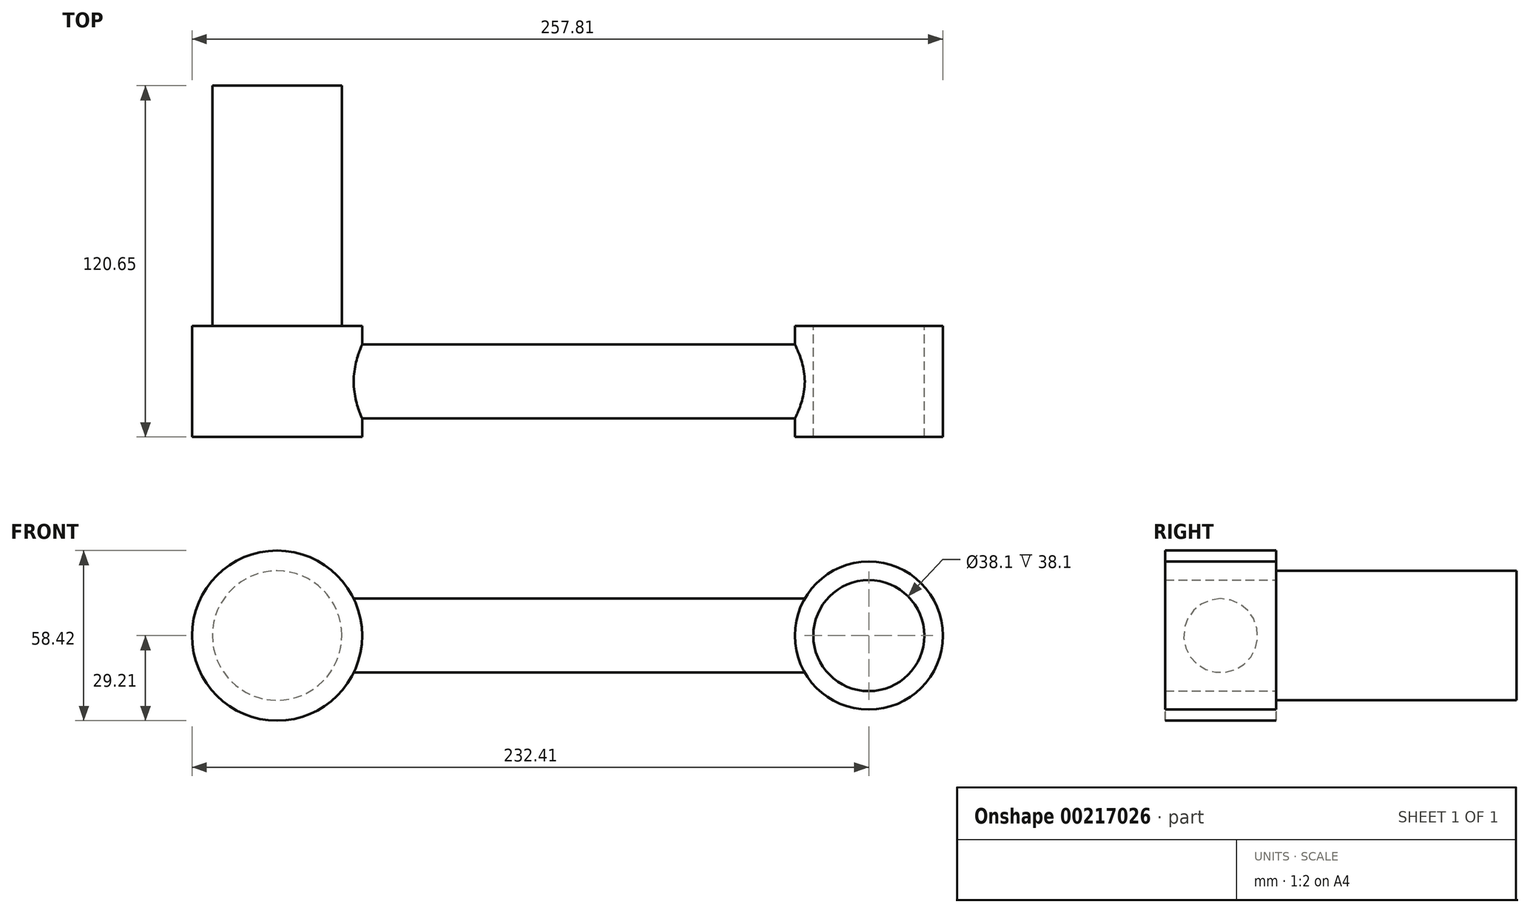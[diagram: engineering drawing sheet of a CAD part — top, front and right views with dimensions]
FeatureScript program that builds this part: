
annotation { "Feature Type Name" : "Feature", "Feature Type Description" : "" }
export const myFeature = defineFeature(function(context is Context, id is Id, definition is map)
    precondition{}
    {
        {
            var Q0;
            Q0=qCreatedBy(makeId("Front.planeOp"),FACE);
            var sketch = newSketch(context, id + "F0", { "sketchPlane" : qUnion([Q0])});
            skLineSegment(sketch, "E0", {"start": v(0, 0) * mm, "end": v(203.2, 0) * mm, "construction": true});
            skCircle(sketch, "E1", {"center": v(0, 0) * mm, "radius": 22.23 * mm});
            skCircle(sketch, "E2", {"center": v(0, 0) * mm, "radius": 29.21 * mm});
            skCircle(sketch, "E3", {"center": v(203.2, 0) * mm, "radius": 19.05 * mm});
            skCircle(sketch, "E4", {"center": v(203.2, 0) * mm, "radius": 25.4 * mm});
            skSolve(sketch);
        }
        {
            var Q0;
            Q0=qCreatedBy(makeId("Right.planeOp"),FACE);
            var sketch = newSketch(context, id + "F1", { "sketchPlane" : qUnion([Q0])});
            skCircle(sketch, "E5", {"center": v(0, 0) * mm, "radius": 12.7 * mm});
            skSolve(sketch);
        }
        {
            var Q0;
            Q0=makeQuery(id+"F0.imprint","IMPRINT",FACE,{"disambiguationData":[TD([[makeQuery(id+"F0.imprint","IMPRINT",EDGE,{"derivedFrom":sQuery(id+"F0.wireOp",EDGE,"E1")}),-1.0]])]});
            var Q1;
            Q1=makeQuery(id+"F0.imprint","IMPRINT",FACE,{"disambiguationData":[TD([[makeQuery(id+"F0.imprint","IMPRINT",EDGE,{"derivedFrom":sQuery(id+"F0.wireOp",EDGE,"E3")}),-1.0]])]});
            extrude(context, id + "F2", {"entities" : qUnion([Q0, Q1]), "depth" : 38.1 * mm, "symmetric" : true});
        }
        {
            var Q0;
            Q0=makeQuery(id+"F1.imprint","IMPRINT",FACE,{"disambiguationData":[TD([[makeQuery(id+"F1.imprint","IMPRINT",EDGE,{"derivedFrom":sQuery(id+"F1.wireOp",EDGE,"E5")}),1.0]])]});
            var Q1;
            Q1=sQuery(id+"F1.wireOp",EDGE,"E5");
            var Q2;
            Q2=makeQuery(id+"F2.opExtrude","SWEPT_FACE",FACE,{"disambiguationData":[OSD([sQuery(id+"F0.wireOp",EDGE,"E4")])]});
            var Q3;
            Q3=makeQuery(id+"F2.opExtrude","SWEPT_FACE",FACE,{"disambiguationData":[OSD([sQuery(id+"F0.wireOp",EDGE,"E2")])]});
            extrude(context, id + "F3", {"entities" : qUnion([Q0]), "operationType" : NewBodyOperationType.ADD, "surfaceEntities" : qUnion([Q1]), "endBound" : BoundingType.UP_TO_SURFACE, "endBoundEntityFace" : qUnion([Q2]), "depth" : 25.4 * mm, "hasSecondDirection" : true, "secondDirectionBound" : BoundingType.UP_TO_SURFACE, "secondDirectionOppositeDirection" : false, "secondDirectionBoundEntityFace" : qUnion([Q3]), "secondDirectionDepth" : 25.4 * mm});
        }
        {
            var Q0;
            Q0=makeQuery(id+"F0.imprint","IMPRINT",FACE,{"disambiguationData":[TD([[makeQuery(id+"F0.imprint","IMPRINT",EDGE,{"derivedFrom":sQuery(id+"F0.wireOp",EDGE,"E1")}),1.0]])]});
            extrude(context, id + "F4", {"entities" : qUnion([Q0]), "operationType" : NewBodyOperationType.ADD, "depth" : 19.05 * mm, "hasSecondDirection" : true, "secondDirectionOppositeDirection" : true, "secondDirectionDepth" : 101.6 * mm});
        }
    });
